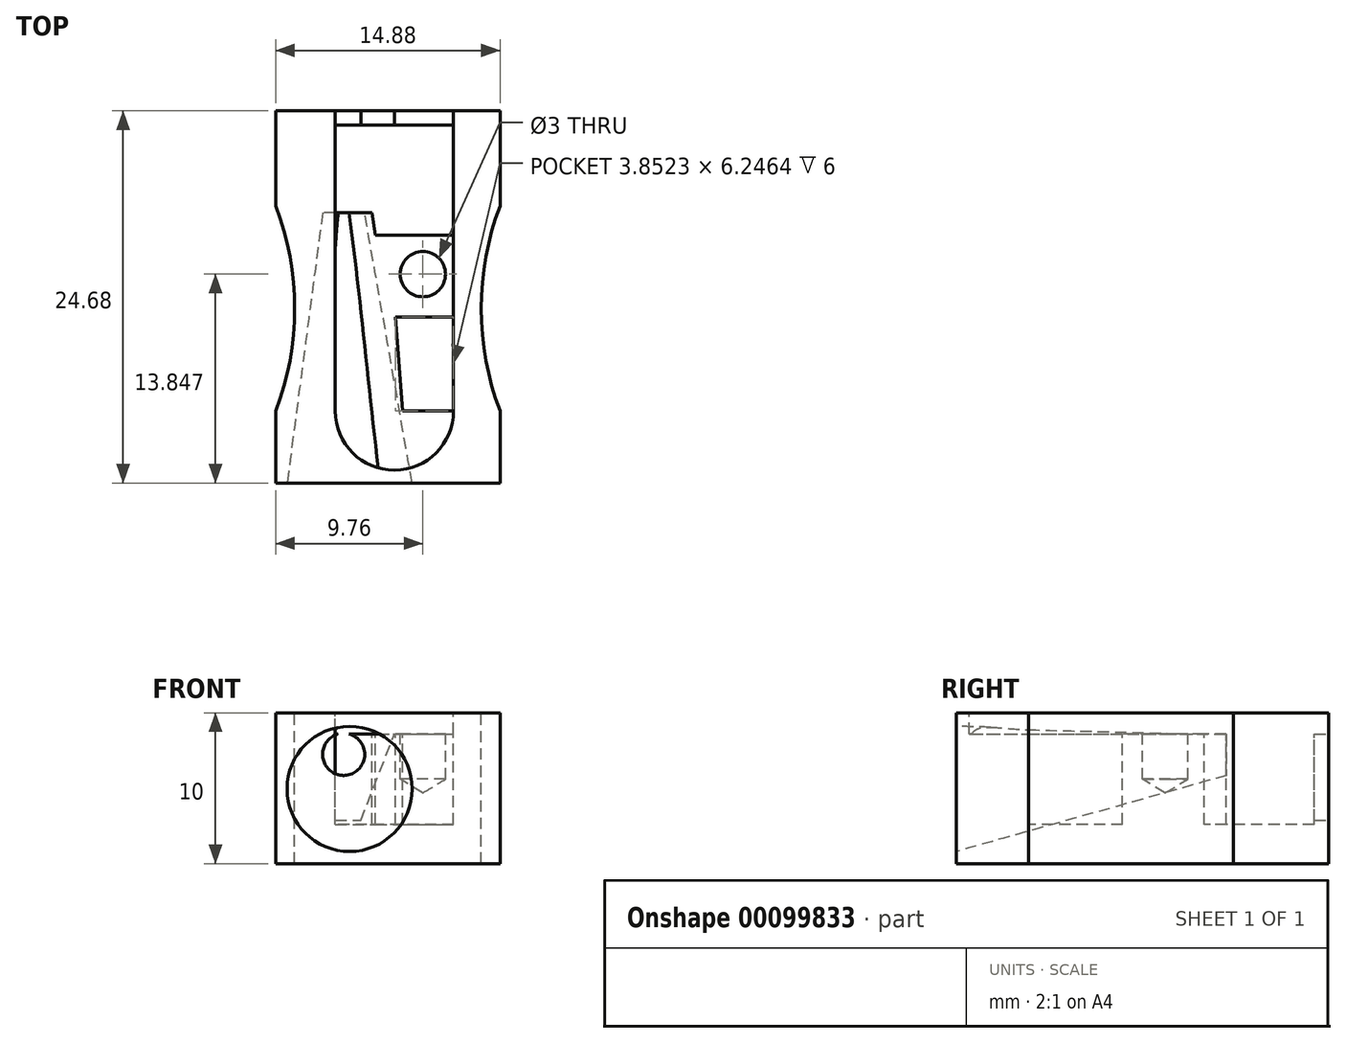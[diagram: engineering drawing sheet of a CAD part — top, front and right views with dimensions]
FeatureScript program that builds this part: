
annotation { "Feature Type Name" : "Feature", "Feature Type Description" : "" }
export const myFeature = defineFeature(function(context is Context, id is Id, definition is map)
    precondition{}
    {
        {
            var Q0;
            Q0=qCreatedBy(makeId("Top.planeOp"),FACE);
            var sketch = newSketch(context, id + "F0", { "sketchPlane" : qUnion([Q0])});
            skLineSegment(sketch, "E0", {"start": v(-7.44, 24.68) * mm, "end": v(-7.44, 0) * mm});
            skLineSegment(sketch, "E1", {"start": v(7.44, 24.68) * mm, "end": v(7.44, 0) * mm});
            skLineSegment(sketch, "E2", {"start": v(-7.44, 24.68) * mm, "end": v(7.44, 24.68) * mm});
            skLineSegment(sketch, "E3", {"start": v(-7.44, 0) * mm, "end": v(0, 0) * mm});
            skLineSegment(sketch, "E4", {"start": v(7.44, 0) * mm, "end": v(0, 0) * mm});
            skSolve(sketch);
        }
        {
            var Q0;
            Q0 = qSketchRegion(id + "F0", true);
            extrude(context, id + "F1", {"entities" : qUnion([Q0]), "depth" : 10 * mm});
        }
        {
            var Q0;
            Q0=makeQuery(id+"F1.opExtrude","CAP_FACE",FACE,{"disambiguationData":[OSD([sQuery(id+"F0.wireOp",EDGE,"E0"),sQuery(id+"F0.wireOp",EDGE,"E1"),sQuery(id+"F0.wireOp",EDGE,"E2"),sQuery(id+"F0.wireOp",EDGE,"E3"),sQuery(id+"F0.wireOp",EDGE,"E4")])],"isStart":false});
            var sketch = newSketch(context, id + "F2", { "sketchPlane" : qUnion([Q0])});
            skLineSegment(sketch, "E5", {"start": v(-3.5, 24.68) * mm, "end": v(-3.5, 4.77) * mm});
            skLineSegment(sketch, "E6", {"start": v(4.35, 24.68) * mm, "end": v(4.35, 4.77) * mm});
            skArc(sketch, "E7", {"start": v(-3.5, 4.77) * mm, "mid": v(0.43, 0.85) * mm, "end": v(4.35, 4.77) * mm});
            skLineSegment(sketch, "E8", {"start": v(4.35, 24.68) * mm, "end": v(-3.5, 24.68) * mm});
            skSolve(sketch);
        }
        {
            var Q0;
            Q0=makeQuery(id+"F2.imprint","IMPRINT",FACE,{"disambiguationData":[TD([[makeQuery(id+"F2.imprint","IMPRINT",EDGE,{"derivedFrom":sQuery(id+"F2.wireOp",EDGE,"E5")}),1.0]])]});
            extrude(context, id + "F3", {"entities" : qUnion([Q0]), "operationType" : NewBodyOperationType.REMOVE, "oppositeDirection" : true, "depth" : 1.4 * mm});
        }
        {
            var Q0;
            Q0=qCreatedBy(makeId("Front.planeOp"),FACE);
            var sketch = newSketch(context, id + "F4", { "sketchPlane" : qUnion([Q0])});
            skCircle(sketch, "E9", {"center": v(-2.54, 4.96) * mm, "radius": 4.15 * mm});
            skSolve(sketch);
        }
        {
            var Q0;
            Q0=qCreatedBy(makeId("Front.planeOp"),FACE);
            cPlane(context, id + "F5", {"entities" : qUnion([Q0]), "cplaneType" : CPlaneType.OFFSET, "offset" : 17.91 * mm, "oppositeDirection" : true, "width" : 150 * mm, "height" : 150 * mm});
        }
        {
            var Q0;
            Q0=qCreatedBy(id+"F5.planeOp",FACE);
            var sketch = newSketch(context, id + "F6", { "sketchPlane" : qUnion([Q0])});
            skCircle(sketch, "E10", {"center": v(-2.94, 7.25) * mm, "radius": 1.4 * mm});
            skSolve(sketch);
        }
        {
            var Q1;
            Q1=makeQuery(id+"F4.imprint","IMPRINT",FACE,{"disambiguationData":[TD([[makeQuery(id+"F4.imprint","IMPRINT",EDGE,{"derivedFrom":sQuery(id+"F4.wireOp",EDGE,"E9")}),1.0]])]});
            var Q2;
            Q2=makeQuery(id+"F6.imprint","IMPRINT",FACE,{"disambiguationData":[TD([[makeQuery(id+"F6.imprint","IMPRINT",EDGE,{"derivedFrom":sQuery(id+"F6.wireOp",EDGE,"E10")}),1.0]])]});
            loft(context, id + "F7", {"operationType" : NewBodyOperationType.REMOVE, "sheetProfilesArray" : [{ "sheetProfileEntities" : qUnion([Q1]) }, { "sheetProfileEntities" : qUnion([Q2]) }]});
        }
        {
            var Q0;
            Q0=makeQuery(id+"F1.opExtrude","CAP_FACE",FACE,{"disambiguationData":[OSD([sQuery(id+"F0.wireOp",EDGE,"E0"),sQuery(id+"F0.wireOp",EDGE,"E1"),sQuery(id+"F0.wireOp",EDGE,"E2"),sQuery(id+"F0.wireOp",EDGE,"E3"),sQuery(id+"F0.wireOp",EDGE,"E4")])],"isStart":false});
            var sketch = newSketch(context, id + "F8", { "sketchPlane" : qUnion([Q0])});
            skArc(sketch, "E11", {"start": v(-7.44, 4.77) * mm, "mid": v(-6.2, 11.57) * mm, "end": v(-7.44, 18.37) * mm});
            skArc(sketch, "E12", {"start": v(7.44, 18.37) * mm, "mid": v(6.19, 11.57) * mm, "end": v(7.44, 4.77) * mm});
            skSolve(sketch);
        }
        {
            var Q0;
            {var subQ0=sQuery(id+"F8.wireOp",EDGE,"E11");Q0=makeQuery(id+"F8.imprint","IMPRINT",FACE,{"disambiguationData":[TD([[makeQuery(id+"F8.imprint","IMPRINT",EDGE,{"derivedFrom":subQ0}),1.0]])]});}
            var Q1;
            {var subQ0=sQuery(id+"F8.wireOp",EDGE,"E12");Q1=makeQuery(id+"F8.imprint","IMPRINT",FACE,{"disambiguationData":[TD([[makeQuery(id+"F8.imprint","IMPRINT",EDGE,{"derivedFrom":subQ0}),1.0]])]});}
            extrude(context, id + "F9", {"entities" : qUnion([Q0, Q1]), "operationType" : NewBodyOperationType.REMOVE, "oppositeDirection" : true, "depth" : 25 * mm});
        }
        {
            var Q0;
            Q0=makeQuery(id+"F3.boolean.opBoolean","COPY",FACE,{"derivedFrom":makeQuery(id+"F3.opExtrude","CAP_FACE",FACE,{"disambiguationData":[OSD([sQuery(id+"F2.wireOp",EDGE,"E5"),sQuery(id+"F2.wireOp",EDGE,"E6"),sQuery(id+"F2.wireOp",EDGE,"E7"),sQuery(id+"F2.wireOp",EDGE,"E8")])],"isStart":false})});
            var sketch = newSketch(context, id + "F10", { "sketchPlane" : qUnion([Q0])});
            skLineSegment(sketch, "E13.bottom", {"start": v(0.98, 4.77) * mm, "end": v(4.35, 4.77) * mm});
            skLineSegment(sketch, "E13.top", {"start": v(0.5, 11.02) * mm, "end": v(4.35, 11.02) * mm});
            skLineSegment(sketch, "E13.left", {"start": v(0.98, 4.77) * mm, "end": v(0.5, 11.02) * mm});
            skLineSegment(sketch, "E13.right", {"start": v(4.35, 4.77) * mm, "end": v(4.35, 11.02) * mm});
            skLineSegment(sketch, "E14", {"start": v(-0.82, 16.42) * mm, "end": v(4.35, 16.42) * mm});
            skLineSegment(sketch, "E15", {"start": v(4.35, 16.42) * mm, "end": v(4.35, 23.74) * mm});
            skLineSegment(sketch, "E16", {"start": v(4.35, 23.74) * mm, "end": v(-3.5, 23.74) * mm});
            skLineSegment(sketch, "E17", {"start": v(-3.5, 23.74) * mm, "end": v(-3.5, 17.91) * mm});
            skPoint(sketch, "E17.endSnap0", {"position": v(-2.94, 17.91) * mm});
            skLineSegment(sketch, "E18", {"start": v(-3.5, 17.91) * mm, "end": v(-1.06, 17.91) * mm});
            skLineSegment(sketch, "E19", {"start": v(-1.06, 17.91) * mm, "end": v(-0.82, 16.42) * mm});
            skSolve(sketch);
        }
        {
            var Q0;
            Q0=makeQuery(id+"F10.imprint","IMPRINT",FACE,{"disambiguationData":[TD([[makeQuery(id+"F10.imprint","IMPRINT",EDGE,{"derivedFrom":sQuery(id+"F10.wireOp",EDGE,"uPt4pLl8-qxVA-BJCW-eppz-jSIWDehlQ4hl")}),1.0]])]});
            var Q1;
            Q1=makeQuery(id+"F10.imprint","IMPRINT",FACE,{"disambiguationData":[TD([[makeQuery(id+"F10.imprint","IMPRINT",EDGE,{"derivedFrom":sQuery(id+"F10.wireOp",EDGE,"E13.bottom")}),1.0]])]});
            extrude(context, id + "F11", {"entities" : qUnion([Q0, Q1]), "operationType" : NewBodyOperationType.REMOVE, "oppositeDirection" : true, "depth" : 6 * mm});
        }
        {
            var Q0;
            Q0 = qSketchRegion(id + "F10", true);
            extrude(context, id + "F12", {"entities" : qUnion([Q0]), "operationType" : NewBodyOperationType.REMOVE, "oppositeDirection" : true, "depth" : 6 * mm});
        }
        {
            var Q0;
            Q0=makeQuery(id+"F1.opExtrude","SWEPT_FACE",FACE,{"disambiguationData":[OSD([sQuery(id+"F0.wireOp",EDGE,"E2")])]});
            var sketch = newSketch(context, id + "F13", { "sketchPlane" : qUnion([Q0])});
            skLineSegment(sketch, "E20", {"start": v(3.49, 8.6) * mm, "end": v(3.49, 2.87) * mm});
            skLineSegment(sketch, "E21", {"start": v(3.49, 2.87) * mm, "end": v(1.8, 2.87) * mm});
            skLineSegment(sketch, "E22", {"start": v(1.8, 2.87) * mm, "end": v(-0.43, 8.6) * mm});
            skSolve(sketch);
        }
        {
            var Q0;
            {var subQ0=sQuery(id+"F13.wireOp",EDGE,"E20");Q0=makeQuery(id+"F13.imprint","IMPRINT",FACE,{"disambiguationData":[TD([[makeQuery(id+"F13.imprint","IMPRINT",EDGE,{"derivedFrom":subQ0}),-1.0]])]});}
            extrude(context, id + "F14", {"entities" : qUnion([Q0]), "operationType" : NewBodyOperationType.REMOVE, "oppositeDirection" : true, "depth" : 6 * mm});
        }
        {
            var Q0;
            {var subQ0=sQuery(id+"F2.wireOp",EDGE,"E6");var subQ1=sQuery(id+"F2.wireOp",EDGE,"E7");Q0=makeQuery(id+"F12.boolean.opBoolean","SPLIT",FACE,{"disambiguationData":[TD([makeQuery(id+"F3.boolean.opBoolean","COPY",FACE,{"derivedFrom":makeQuery(id+"F3.opExtrude","SWEPT_FACE",FACE,{"disambiguationData":[OSD([subQ0])]})}),makeQuery(id+"F3.boolean.opBoolean","COPY",FACE,{"derivedFrom":makeQuery(id+"F3.opExtrude","SWEPT_FACE",FACE,{"disambiguationData":[OSD([subQ1])]})}),makeQuery(id+"F7.boolean.opBoolean","COPY",FACE,{"derivedFrom":makeQuery(id+"F7.opLoft","SWEPT_FACE",FACE,{"disambiguationData":[OSD([sQuery(id+"F4.wireOp",EDGE,"E9"),sQuery(id+"F6.wireOp",EDGE,"E10")])]})}),makeQuery(id+"F11.opExtrude","SWEPT_FACE",FACE,{"disambiguationData":[OSD([sQuery(id+"F10.wireOp",EDGE,"E13.right")])]}),makeQuery(id+"F11.boolean.opBoolean","COPY",FACE,{"derivedFrom":makeQuery(id+"F11.opExtrude","SWEPT_FACE",FACE,{"disambiguationData":[OSD([sQuery(id+"F10.wireOp",EDGE,"E13.bottom")])]})}),makeQuery(id+"F11.boolean.opBoolean","COPY",FACE,{"derivedFrom":makeQuery(id+"F11.opExtrude","SWEPT_FACE",FACE,{"disambiguationData":[OSD([sQuery(id+"F10.wireOp",EDGE,"E13.top")])]})}),makeQuery(id+"F11.boolean.opBoolean","COPY",FACE,{"derivedFrom":makeQuery(id+"F11.opExtrude","SWEPT_FACE",FACE,{"disambiguationData":[OSD([sQuery(id+"F10.wireOp",EDGE,"E13.left")])]})}),makeQuery(id+"F12.opExtrude","SWEPT_FACE",FACE,{"disambiguationData":[OSD([sQuery(id+"F10.wireOp",EDGE,"E14")])]}),makeQuery(id+"F12.opExtrude","SWEPT_FACE",FACE,{"disambiguationData":[OSD([sQuery(id+"F10.wireOp",EDGE,"E15")])]}),makeQuery(id+"F12.opExtrude","SWEPT_FACE",FACE,{"disambiguationData":[OSD([sQuery(id+"F10.wireOp",EDGE,"E18")])]}),makeQuery(id+"F12.opExtrude","SWEPT_FACE",FACE,{"disambiguationData":[OSD([sQuery(id+"F10.wireOp",EDGE,"E19")])]})])],"derivedFrom":makeQuery(id+"F3.boolean.opBoolean","COPY",FACE,{"derivedFrom":makeQuery(id+"F3.opExtrude","CAP_FACE",FACE,{"disambiguationData":[OSD([sQuery(id+"F2.wireOp",EDGE,"E5"),subQ0,subQ1,sQuery(id+"F2.wireOp",EDGE,"E8")])],"isStart":false})})});}
            var sketch = newSketch(context, id + "F15", { "sketchPlane" : qUnion([Q0])});
            skPoint(sketch, "E23", {"position": v(2.32, 13.85) * mm});
            skSolve(sketch);
        }
        {
            var Q0;
            Q0=sQuery(id+"F15.wireOp",VERTEX,"E23");
            var Q1;
            Q1=makeQuery(id+"F1.opExtrude","SWEPT_BODY",BODY,{"disambiguationData":[OSD([sQuery(id+"F0.wireOp",EDGE,"E0"),sQuery(id+"F0.wireOp",EDGE,"E1"),sQuery(id+"F0.wireOp",EDGE,"E2"),sQuery(id+"F0.wireOp",EDGE,"E3"),sQuery(id+"F0.wireOp",EDGE,"E4")])]});
            hole(context, id + "F16", {"style" : HoleStyle.C_BORE, "endStyle" : HoleEndStyle.BLIND, "holeDiameter" : 3 * mm, "cBoreDiameter" : 3 * mm, "cBoreDepth" : 3 * mm, "holeDepth" : 3 * mm, "locations" : qUnion([Q0]), "scope" : qUnion([Q1])});
        }
    });
